# Revit family: Deca_Coluna suspensa para lavatório_Cubas Apoio_C.69
name_source: partatom
category: Plumbing Fixtures
units: mm (PartAtom-declared; Revit-internal decimal feet)

## family parameters
Cut with Voids When Loaded = No
Host = Face
Part Type = Normal
Room Calculation Point = No
Round Connector Dimension = Use Diameter
Shared = Yes

## types (1)
- C.69.17_Branco
    Acompanha o Produto = CONJUNTO DE FIX. COLUNA C69 (34423)
    Aprovado por = quattroD
    Atendimento ao Cliente = 0800-0117073
    Categoria = CUBAS
    Composição Anel Vedação = -
    Composição Assento = -
    Composição Básica = Argila, feldspato, caulim, vidrados e corantes inorgânicos.
    Composição Componente = Liga de cobre (bronze e latão), elastômeros e plásticos de engenharia.
    Consumo = -
    Cor Interna = -
    Cor Principal = Branco
    Cor Secundária = -
    Cores Componente = Não Possui
    Criado por = quattroD
    Código Pai = C.69
    Default Elevation = 0 mm  [stored 0 ft]
    Description = Coluna suspensa para lavatório
    Informações Complementares = -
    Itens de Instalação = -
    Linha = Cubas Apoio
    Manufacturer = Deca
    Material = Deca_Branco
    Model = C.69.17
    Norma = NBR-16728-1;NBR-16728-2
    Peso Líquido (Kg) = 6.708
    Pressão máx. funcionamento = -
    Pressão mín. Aquec. Acúmulo = -
    Pressão mín. Aquec. Passagem = -
    Pressão mín. funcionamento = -
    Saída de Esgoto = -
    Segmento = Banheiro Luxo
    Tipo de dispositivo economizador = -
    Tipo de mecanismo utilizado = -
    Tipo de rosca de entrada = -
    Tipo de rosca de saída = -
    URL = www.deca.com.br
    Vazão na Pressão máx. (L/min) = -
    Vazão na Pressão mín. (L/min) = -

note: [stored X ft] marks values corroborated as IEEE doubles in the binary element streams (Revit-internal decimal feet)

## geometry (parser evidence)
native form markers: Sweep x3
no freeform markers — native parametric forms only
